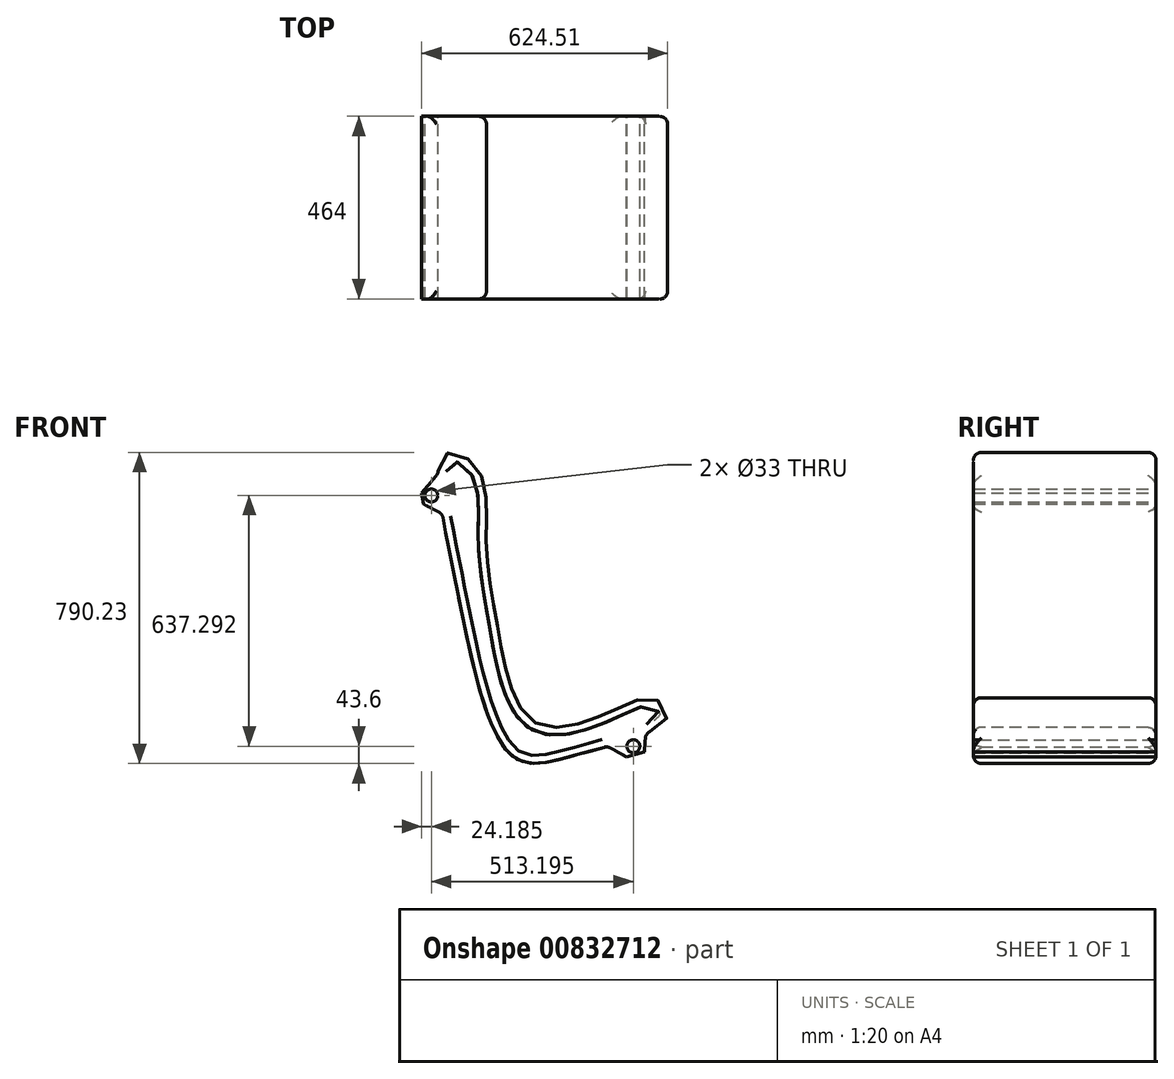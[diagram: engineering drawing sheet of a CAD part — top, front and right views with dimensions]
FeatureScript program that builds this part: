
annotation { "Feature Type Name" : "Feature", "Feature Type Description" : "" }
export const myFeature = defineFeature(function(context is Context, id is Id, definition is map)
    precondition{}
    {
        {
            var Q0;
            Q0=qCreatedBy(makeId("Front.planeOp"),FACE);
            var sketch = newSketch(context, id + "F0", { "sketchPlane" : qUnion([Q0])});
            skCircle(sketch, "E0", {"center": v(0, 0) * mm, "radius": 16.5 * mm});
            skCircle(sketch, "E1", {"center": v(-513.2, 637.3) * mm, "radius": 16.5 * mm});
            skFitSpline(sketch, "E2", {"points": [v(-478.55, 742.94) * mm, v(-394.54, 702.79) * mm, v(-374.05, 535.24) * mm, v(-344.9, 302.62) * mm, v(-247.07, 58.44) * mm, v(-40.47, 96.2) * mm, v(54.45, 120.3) * mm, v(85.72, 72.94) * mm, v(-140.85, -20.62) * mm, v(-310, -22.75) * mm, v(-456.44, 442.78) * mm, v(-478.55, 742.94) * mm]});
            skLineSegment(sketch, "E3", {"start": v(31.57, 32.59) * mm, "end": v(27.94, -13.64) * mm});
            skLineSegment(sketch, "E4", {"start": v(27.94, -13.64) * mm, "end": v(-17.1, -26.97) * mm});
            skLineSegment(sketch, "E5", {"start": v(-17.1, -26.97) * mm, "end": v(-65.72, 0) * mm});
            skLineSegment(sketch, "E6", {"start": v(-496.1, 693.19) * mm, "end": v(-537.38, 643.54) * mm});
            skLineSegment(sketch, "E7", {"start": v(-537.38, 643.54) * mm, "end": v(-533.61, 615.4) * mm});
            skLineSegment(sketch, "E8", {"start": v(-533.61, 615.4) * mm, "end": v(-485.5, 590.94) * mm});
            skSolve(sketch);
        }
        {
            var Q0;
            Q0 = qSketchRegion(id + "F0", true);
            extrude(context, id + "F1", {"entities" : qUnion([Q0]), "depth" : 464 * mm, "offsetDistance" : 25 * mm});
        }
        {
            var Q0;
            {var subQ0=sQuery(id+"F0.wireOp",EDGE,"E2");Q0=makeQuery(id+"F1.opExtrude","SWEPT_FACE",FACE,{"disambiguationData":[OSD([subQ0]),TDD([makeQuery(id+"F0.imprint","IMPRINT",EDGE,{"disambiguationData":[TD([[makeQuery(id+"F0.imprint","INTERSECT",VERTEX,{"derivedFrom":[subQ0,sQuery(id+"F0.wireOp",EDGE,"E3")]}),1.0]])],"derivedFrom":subQ0})])]});}
            var Q1;
            {var subQ0=sQuery(id+"F0.wireOp",EDGE,"E2");Q1=makeQuery(id+"F1.opExtrude","SWEPT_FACE",FACE,{"disambiguationData":[OSD([subQ0]),TDD([makeQuery(id+"F0.imprint","IMPRINT",EDGE,{"disambiguationData":[TD([[makeQuery(id+"F0.imprint","INTERSECT",VERTEX,{"derivedFrom":[subQ0,sQuery(id+"F0.wireOp",EDGE,"E5")]}),-1.0]])],"derivedFrom":subQ0})])]});}
            fillet(context, id + "F2", {"entities" : qUnion([Q0, Q1]), "radius" : 20 * mm, "tangentPropagation" : true, "allowEdgeOverflow" : false});
        }
    });
